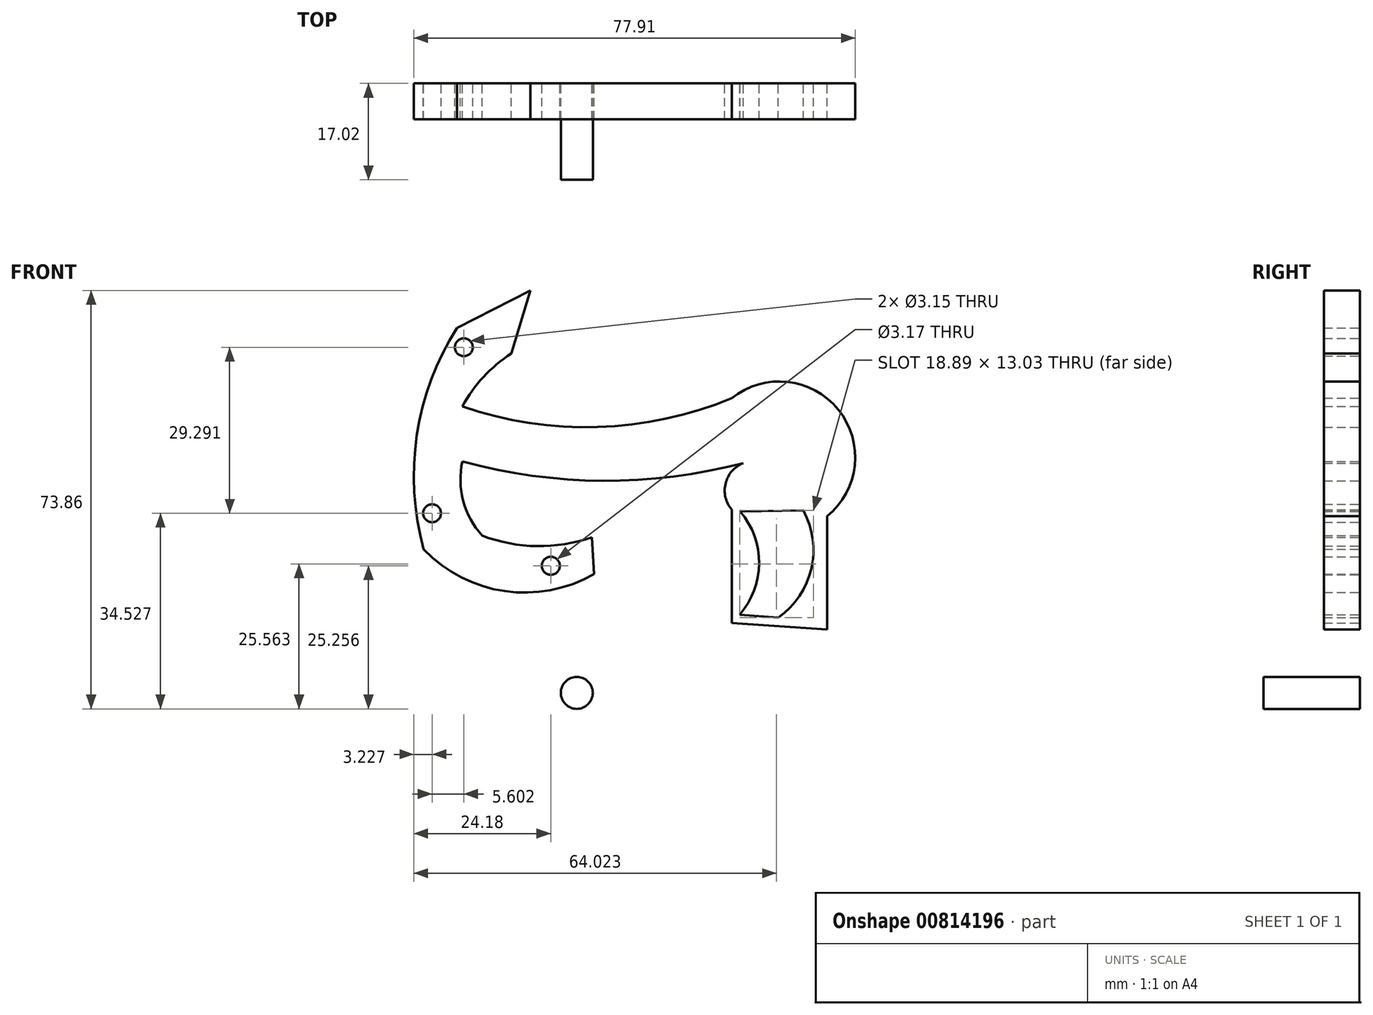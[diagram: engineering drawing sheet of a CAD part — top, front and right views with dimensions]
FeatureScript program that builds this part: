
annotation { "Feature Type Name" : "Feature", "Feature Type Description" : "" }
export const myFeature = defineFeature(function(context is Context, id is Id, definition is map)
    precondition{}
    {
        {
            var Q0;
            Q0=qCreatedBy(makeId("Front.planeOp"),FACE);
            var sketch = newSketch(context, id + "F0", { "sketchPlane" : qUnion([Q0])});
            skLineSegment(sketch, "E0", {"start": v(-8.2, -8.53) * mm, "end": v(-8.2, -28.53) * mm});
            skLineSegment(sketch, "E1", {"start": v(8.61, -9.7) * mm, "end": v(8.61, -29.7) * mm});
            skLineSegment(sketch, "E2", {"start": v(-8.2, -28.53) * mm, "end": v(8.61, -29.7) * mm});
            skArc(sketch, "E3", {"start": v(-55.75, 0) * mm, "mid": v(-30.38, -3.43) * mm, "end": v(-5, 0) * mm});
            skArc(sketch, "E4", {"start": v(-60.15, 11.4) * mm, "mid": v(-34.2, 6.02) * mm, "end": v(-8.2, 11.13) * mm});
            skPoint(sketch, "E4.endSnap0", {"position": v(-8.2, -18.53) * mm});
            skLineSegment(sketch, "E5", {"start": v(-60.15, 11.4) * mm, "end": v(-55.75, 0) * mm});
            skArc(sketch, "E6", {"start": v(-56.69, 23.5) * mm, "mid": v(-63.78, 4.61) * mm, "end": v(-62.57, -15.53) * mm});
            skLineSegment(sketch, "E7", {"start": v(-56.69, 23.5) * mm, "end": v(-43.77, 30.17) * mm});
            skLineSegment(sketch, "E8", {"start": v(-43.77, 30.17) * mm, "end": v(-47.12, 19) * mm});
            skArc(sketch, "E9", {"start": v(-52.27, -13.1) * mm, "mid": v(-42.6, -14.96) * mm, "end": v(-32.89, -13.41) * mm});
            skArc(sketch, "E10", {"start": v(-62.57, -15.53) * mm, "mid": v(-48.28, -22.9) * mm, "end": v(-32.48, -19.87) * mm});
            skLineSegment(sketch, "E11", {"start": v(-32.89, -13.41) * mm, "end": v(-32.48, -19.87) * mm});
            skCircle(sketch, "E12", {"center": v(-40.14, -18.43) * mm, "radius": 1.59 * mm});
            skCircle(sketch, "E13", {"center": v(-35.55, -40.86) * mm, "radius": 2.83 * mm});
            skPoint(sketch, "E14", {"position": v(-55.75, 9.7) * mm});
            skArc(sketch, "E15", {"start": v(-47.12, 19) * mm, "mid": v(-52.02, 14.9) * mm, "end": v(-55.75, 9.7) * mm});
            skArc(sketch, "E16", {"start": v(-55.75, 0) * mm, "mid": v(-55.6, -6.97) * mm, "end": v(-52.27, -13.1) * mm});
            skPoint(sketch, "E17", {"position": v(-8.2, -8.53) * mm});
            skPoint(sketch, "E18", {"position": v(8.61, -9.7) * mm});
            skArc(sketch, "E19", {"start": v(8.61, -9.7) * mm, "mid": v(10.63, 9.12) * mm, "end": v(-8.2, 11.13) * mm});
            skArc(sketch, "E20", {"start": v(-5, 0) * mm, "mid": v(-9.11, -3.32) * mm, "end": v(-8.2, -8.53) * mm});
            skCircle(sketch, "E21", {"center": v(-55.5, 20.13) * mm, "radius": 1.58 * mm});
            skCircle(sketch, "E22", {"center": v(-61.1, -9.16) * mm, "radius": 1.58 * mm});
            skArc(sketch, "E23", {"start": v(-6.81, -27.1) * mm, "mid": v(-3.36, -17.99) * mm, "end": v(-6.7, -8.84) * mm});
            skArc(sketch, "E24", {"start": v(0, -27.57) * mm, "mid": v(5.85, -18.98) * mm, "end": v(4.43, -8.68) * mm});
            skLineSegment(sketch, "E25", {"start": v(-6.7, -8.84) * mm, "end": v(4.43, -8.68) * mm});
            skLineSegment(sketch, "E26", {"start": v(-6.81, -27.1) * mm, "end": v(0, -27.57) * mm});
            skSolve(sketch);
        }
        {
            var Q0;
            Q0=makeQuery(id+"F0.imprint","IMPRINT",FACE,{"disambiguationData":[TD([[makeQuery(id+"F0.imprint","IMPRINT",EDGE,{"derivedFrom":sQuery(id+"F0.wireOp",EDGE,"E7")}),-1.0]])]});
            var Q1;
            Q1=makeQuery(id+"F0.imprint","IMPRINT",FACE,{"disambiguationData":[TD([[makeQuery(id+"F0.imprint","IMPRINT",EDGE,{"derivedFrom":sQuery(id+"F0.wireOp",EDGE,"E6")}),1.0]])]});
            var Q2;
            {var subQ2=sQuery(id+"F0.wireOp",EDGE,"E3");Q2=makeQuery(id+"F0.imprint","IMPRINT",FACE,{"disambiguationData":[TD([[makeQuery(id+"F0.imprint","IMPRINT",EDGE,{"derivedFrom":subQ2}),1.0]])]});}
            var Q3;
            {var subQ0=sQuery(id+"F0.wireOp",EDGE,"76u8OsDD-qOSm-tdD2-mYx7-YpV9yENEMW65");var subQ1=makeQuery(id+"F0.imprint","INTERSECT",VERTEX,{"derivedFrom":[subQ0,sQuery(id+"F0.wireOp",EDGE,"E3")]});Q3=makeQuery(id+"F0.imprint","IMPRINT",FACE,{"disambiguationData":[TD([[makeQuery(id+"F0.imprint","IMPRINT",EDGE,{"disambiguationData":[TD([[subQ1,1.0]])],"derivedFrom":subQ0}),1.0]])]});}
            var Q4;
            {var subQ0=sQuery(id+"F0.wireOp",EDGE,"E0");Q4=makeQuery(id+"F0.imprint","IMPRINT",FACE,{"disambiguationData":[TD([[makeQuery(id+"F0.imprint","IMPRINT",EDGE,{"derivedFrom":subQ0}),1.0]])]});}
            var Q5;
            {var subQ0=sQuery(id+"F0.wireOp",EDGE,"E5");Q5=makeQuery(id+"F0.imprint","IMPRINT",FACE,{"disambiguationData":[TD([[makeQuery(id+"F0.imprint","IMPRINT",EDGE,{"derivedFrom":subQ0}),1.0]])]});}
            extrude(context, id + "F1", {"entities" : qUnion([Q0, Q1, Q2, Q3, Q4, Q5]), "depth" : 6.35 * mm, "offsetDistance" : 25.4 * mm});
        }
        {
            var Q0;
            Q0=makeQuery(id+"F0.imprint","IMPRINT",FACE,{"disambiguationData":[TD([[makeQuery(id+"F0.imprint","IMPRINT",EDGE,{"derivedFrom":sQuery(id+"F0.wireOp",EDGE,"E13")}),1.0]])]});
            extrude(context, id + "F2", {"entities" : qUnion([Q0]), "depth" : 17.02 * mm, "offsetDistance" : 25.4 * mm});
        }
    });
